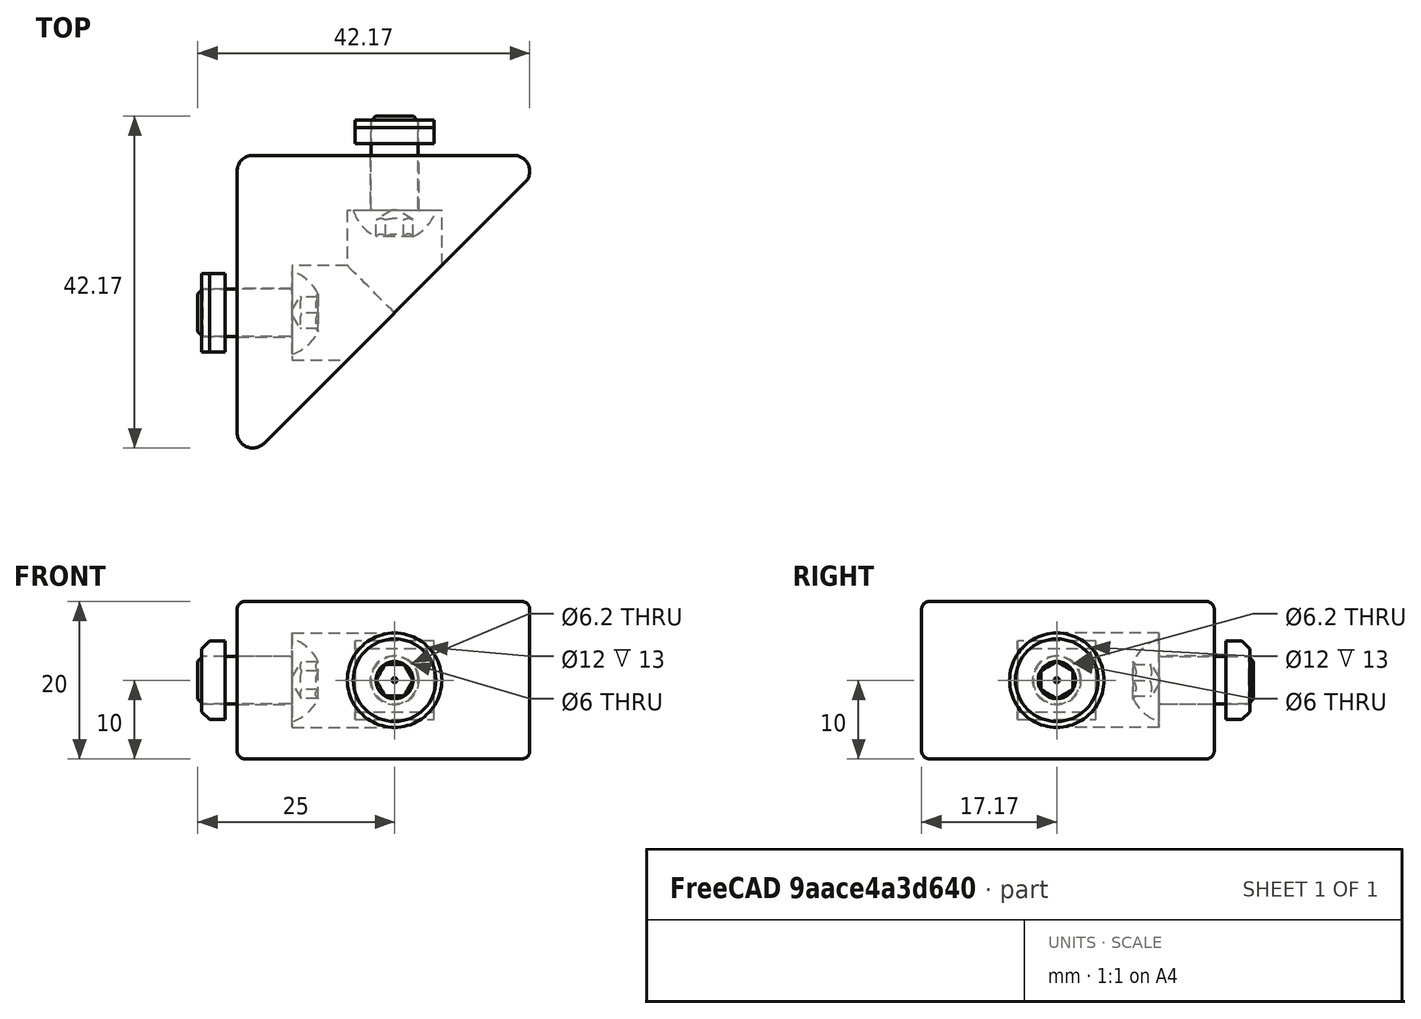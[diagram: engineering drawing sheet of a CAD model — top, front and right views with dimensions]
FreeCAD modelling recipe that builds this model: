
FCSTD DOCUMENT  (FreeCAD 0.17R9796 (Git))
Label: cornerstonescrewnut
License: All rights reserved
LicenseURL: http://en.wikipedia.org/wiki/All_rights_reserved
objects: Part::Feature×3, Part::FeaturePython×2, App::Part×1
note: 5 computed .brp shape members not serialized (recipe doc carries the construction recipe); baked Part::Feature solids carry a one-line shape summary decoded from their .brp

FEATURE [Part::Feature] Fillet004001  label="Fillet005"
  shape: bbox 37.5 x 37.5 x 20 mm, 26 faces (baked)
FEATURE [Part::FeaturePython] Screw  label="M6x12-Screw"  # Fasteners workbench fastener (typed FeaturePython)
  Placement = pos=(7,20,10) rot=(0,1,0;1.5708rad)
  diameter = 4
  invert = false
  length = 1
  matchOuter = false
  offset = 0
  thread = false
  type = 20
FEATURE [Part::Feature] Body001  label="m6nutplate"
  Placement = pos=(-1.5,15,5) rot=(0,1,0;4.71239rad)
  shape: bbox 3 x 10 x 10 mm, 9 faces (baked)
FEATURE [Part::FeaturePython] Screw001  label="M6x12-Screw001"  # Fasteners workbench fastener (typed FeaturePython)
  Placement = pos=(20,33,10) rot=(1,0,0;1.5708rad)
  diameter = 4
  invert = false
  length = 1
  matchOuter = false
  offset = 0
  thread = false
  type = 20
FEATURE [Part::Feature] Body002  label="m6nutplate001"
  Placement = pos=(15,41.5,5) rot=(-0.57735,-0.57735,-0.57735;2.0944rad)
  shape: bbox 10 x 3 x 10 mm, 9 faces (baked)
FEATURE [App::Part] Part
  Group = -> [Body001,Screw,Fillet004001,Screw001,Body002]
  License = CC BY 3.0
  LicenseURL = http://creativecommons.org/licenses/by/3.0/
  Origin = -> PartOrigin
